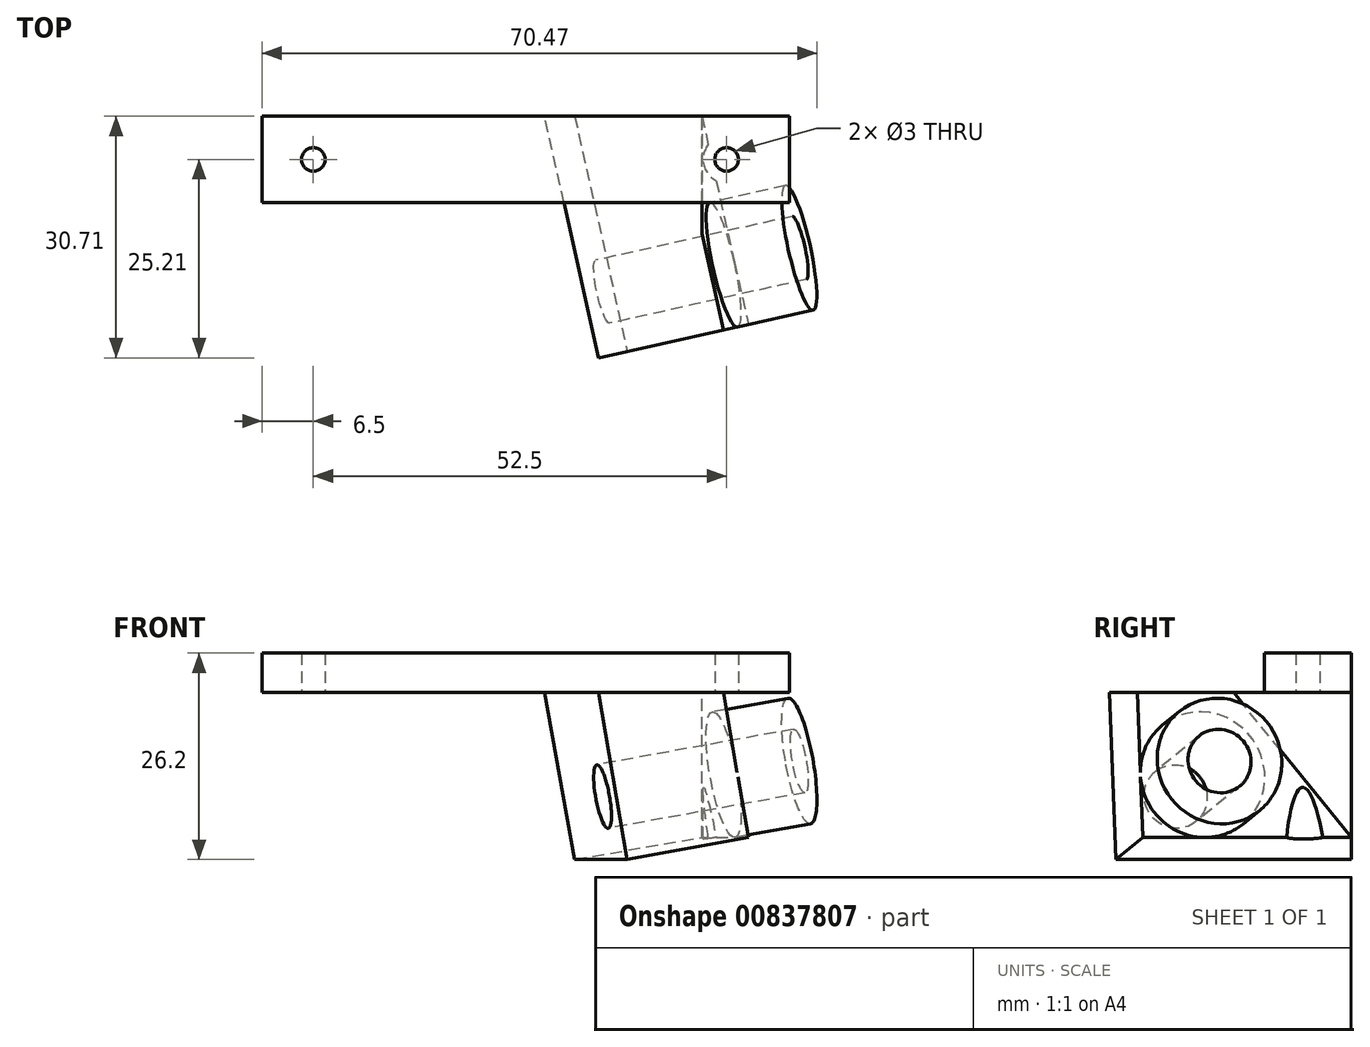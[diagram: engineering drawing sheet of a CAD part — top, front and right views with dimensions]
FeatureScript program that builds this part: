
annotation { "Feature Type Name" : "Feature", "Feature Type Description" : "" }
export const myFeature = defineFeature(function(context is Context, id is Id, definition is map)
    precondition{}
    {
        {
            var Q0;
            Q0=qCreatedBy(makeId("Top.planeOp"),FACE);
            var sketch = newSketch(context, id + "F0", { "sketchPlane" : qUnion([Q0])});
            skLineSegment(sketch, "E0.bottom", {"start": v(37.5, 5.5) * mm, "end": v(-37.5, 5.5) * mm});
            skLineSegment(sketch, "E0.top", {"start": v(37.5, -5.5) * mm, "end": v(-37.5, -5.5) * mm});
            skLineSegment(sketch, "E0.left", {"start": v(37.5, 5.5) * mm, "end": v(37.5, -5.5) * mm});
            skLineSegment(sketch, "E0.right", {"start": v(-37.5, 5.5) * mm, "end": v(-37.5, -5.5) * mm});
            skPoint(sketch, "E0.middle", {"position": v(0, 0) * mm});
            skLineSegment(sketch, "E1", {"start": v(0, 0) * mm, "end": v(-15, 0) * mm, "construction": true});
            skLineSegment(sketch, "E2", {"start": v(0, 0) * mm, "end": v(15, 0) * mm, "construction": true});
            skLineSegment(sketch, "E3", {"start": v(-15, 0) * mm, "end": v(-26.25, 0) * mm, "construction": true});
            skLineSegment(sketch, "E4", {"start": v(15, 0) * mm, "end": v(26.25, 0) * mm, "construction": true});
            skCircle(sketch, "E5", {"center": v(-26.25, 0) * mm, "radius": 1.5 * mm});
            skCircle(sketch, "E6", {"center": v(26.25, 0) * mm, "radius": 1.5 * mm});
            skLineSegment(sketch, "E7", {"start": v(-37.5, 5.5) * mm, "end": v(-43.1, -5.5) * mm, "construction": true});
            skLineSegment(sketch, "E8", {"start": v(-37.5, -5.5) * mm, "end": v(-43.1, -5.5) * mm, "construction": true});
            skLineSegment(sketch, "E9", {"start": v(77.8, 6.5) * mm, "end": v(-101.6, -33.5) * mm, "construction": true});
            skLineSegment(sketch, "E10", {"start": v(-101.6, -33.5) * mm, "end": v(-99.87, -41.3) * mm, "construction": true});
            skLineSegment(sketch, "E11", {"start": v(-99.87, -41.3) * mm, "end": v(79.55, -1.3) * mm, "construction": true});
            skLineSegment(sketch, "E12", {"start": v(77.8, 6.5) * mm, "end": v(79.55, -1.3) * mm, "construction": true});
            skLineSegment(sketch, "E13", {"start": v(24.75, 0) * mm, "end": v(20.75, 0) * mm, "construction": true});
            skLineSegment(sketch, "E14", {"start": v(20.75, 0) * mm, "end": v(23.81, -13.73) * mm, "construction": true});
            skLineSegment(sketch, "E15", {"start": v(20.75, 0) * mm, "end": v(19.52, 5.5) * mm, "construction": true});
            skLineSegment(sketch, "E16", {"start": v(20.75, 0) * mm, "end": v(5.13, -3.48) * mm, "construction": true});
            skLineSegment(sketch, "E17", {"start": v(5.13, -3.48) * mm, "end": v(8.2, -17.2) * mm, "construction": true});
            skLineSegment(sketch, "E18", {"start": v(5.13, -3.48) * mm, "end": v(3.13, 5.5) * mm, "construction": true});
            skLineSegment(sketch, "E19", {"start": v(23.81, -13.73) * mm, "end": v(24.72, -17.82) * mm, "construction": true});
            skLineSegment(sketch, "E20", {"start": v(8.2, -17.2) * mm, "end": v(9.1, -21.3) * mm, "construction": true});
            skLineSegment(sketch, "E21", {"start": v(24.72, -17.82) * mm, "end": v(9.1, -21.3) * mm});
            skLineSegment(sketch, "E22", {"start": v(19.52, 5.5) * mm, "end": v(24.72, -17.82) * mm});
            skLineSegment(sketch, "E23", {"start": v(9.1, -21.3) * mm, "end": v(3.13, 5.5) * mm});
            skLineSegment(sketch, "E24", {"start": v(37.5, 5.5) * mm, "end": v(37.5, 9.6) * mm});
            skLineSegment(sketch, "E25", {"start": v(37.5, 9.6) * mm, "end": v(-37.23, 9.6) * mm});
            skLineSegment(sketch, "E26", {"start": v(-37.23, 9.6) * mm, "end": v(-37.5, 5.5) * mm});
            skCircle(sketch, "E27", {"center": v(26.25, 0) * mm, "radius": 3 * mm});
            skLineSegment(sketch, "E28", {"start": v(29.25, 0) * mm, "end": v(34.25, 0) * mm, "construction": true});
            skLineSegment(sketch, "E29", {"start": v(34.25, 0) * mm, "end": v(34.25, 9.6) * mm, "construction": true});
            skLineSegment(sketch, "E30", {"start": v(34.25, 0) * mm, "end": v(34.25, -5.5) * mm, "construction": true});
            skLineSegment(sketch, "E31", {"start": v(-27.75, 0) * mm, "end": v(-32.75, 0) * mm, "construction": true});
            skLineSegment(sketch, "E32", {"start": v(-32.75, 0) * mm, "end": v(-32.75, 9.6) * mm, "construction": true});
            skLineSegment(sketch, "E33", {"start": v(-32.75, 0) * mm, "end": v(-32.75, -5.5) * mm, "construction": true});
            skLineSegment(sketch, "E34", {"start": v(34.25, 5.5) * mm, "end": v(34.25, -5.5) * mm});
            skLineSegment(sketch, "E35", {"start": v(-32.75, 5.5) * mm, "end": v(-32.75, -5.5) * mm});
            skSolve(sketch);
        }
        {
            var Q0;
            {var subQ5=sQuery(id+"F0.wireOp",EDGE,"E21");Q0=makeQuery(id+"F0.imprint","IMPRINT",FACE,{"disambiguationData":[TD([[makeQuery(id+"F0.imprint","IMPRINT",EDGE,{"derivedFrom":subQ5}),-1.0]])]});}
            var Q1;
            {var subQ0=sQuery(id+"F0.wireOp",EDGE,"E22");var subQ1=sQuery(id+"F0.wireOp",EDGE,"E0.bottom");var subQ2=makeQuery(id+"F0.imprint","INTERSECT",VERTEX,{"derivedFrom":[subQ1,subQ0]});Q1=makeQuery(id+"F0.imprint","IMPRINT",FACE,{"disambiguationData":[TD([[makeQuery(id+"F0.imprint","IMPRINT",EDGE,{"disambiguationData":[TD([[subQ2,-1.0]])],"derivedFrom":subQ1}),1.0]])]});}
            var Q2;
            Q2=makeQuery(id+"F0.imprint","IMPRINT",FACE,{"disambiguationData":[TD([[makeQuery(id+"F0.imprint","IMPRINT",EDGE,{"derivedFrom":sQuery(id+"F0.wireOp",EDGE,"E6")}),-1.0]])]});
            var Q3;
            Q3=makeQuery(id+"F0.imprint","IMPRINT",FACE,{"disambiguationData":[TD([[makeQuery(id+"F0.imprint","IMPRINT",EDGE,{"derivedFrom":sQuery(id+"F0.wireOp",EDGE,"E27")}),-1.0]])]});
            var Q4;
            Q4=makeQuery(id+"F0.imprint","IMPRINT",FACE,{"disambiguationData":[TD([[makeQuery(id+"F0.imprint","IMPRINT",EDGE,{"derivedFrom":sQuery(id+"F0.wireOp",EDGE,"E5")}),-1.0]])]});
            extrude(context, id + "F1", {"entities" : qUnion([Q0, Q1, Q2, Q3, Q4]), "depth" : 5 * mm, "offsetDistance" : 25 * mm});
        }
        {
            var Q0;
            {var subQ0=sQuery(id+"F0.wireOp",EDGE,"E22");var subQ1=sQuery(id+"F0.wireOp",EDGE,"E0.bottom");var subQ2=makeQuery(id+"F0.imprint","INTERSECT",VERTEX,{"derivedFrom":[subQ1,subQ0]});Q0=makeQuery(id+"F0.imprint","IMPRINT",FACE,{"disambiguationData":[TD([[makeQuery(id+"F0.imprint","IMPRINT",EDGE,{"disambiguationData":[TD([[subQ2,-1.0]])],"derivedFrom":subQ1}),1.0]])]});}
            var Q1;
            {var subQ5=sQuery(id+"F0.wireOp",EDGE,"E21");Q1=makeQuery(id+"F0.imprint","IMPRINT",FACE,{"disambiguationData":[TD([[makeQuery(id+"F0.imprint","IMPRINT",EDGE,{"derivedFrom":subQ5}),-1.0]])]});}
            extrude(context, id + "F2", {"entities" : qUnion([Q0, Q1]), "operationType" : NewBodyOperationType.ADD, "oppositeDirection" : true, "depth" : 21.2 * mm, "offsetDistance" : 25 * mm});
        }
        {
            var Q0;
            {var subQ5=sQuery(id+"F0.wireOp",EDGE,"E21");Q0=makeQuery(id+"F0.imprint","IMPRINT",FACE,{"disambiguationData":[TD([[makeQuery(id+"F0.imprint","IMPRINT",EDGE,{"derivedFrom":subQ5}),-1.0]])]});}
            extrude(context, id + "F3", {"entities" : qUnion([Q0]), "operationType" : NewBodyOperationType.REMOVE, "depth" : 5 * mm, "offsetDistance" : 25 * mm});
        }
        {
            var Q0;
            {var subQ0=sQuery(id+"F0.wireOp",EDGE,"E21");Q0=makeQuery(id+"F2.boolean.opBoolean","MERGE",FACE,{"derivedFrom":[makeQuery(id+"F1.opExtrude","SWEPT_FACE",FACE,{"disambiguationData":[OSD([subQ0])]}),makeQuery(id+"F2.opExtrude","SWEPT_FACE",FACE,{"disambiguationData":[OSD([subQ0])]})]});}
            var sketch = newSketch(context, id + "F4", { "sketchPlane" : qUnion([Q0])});
            skLineSegment(sketch, "E36", {"start": v(4.25, 0) * mm, "end": v(8, -21.2) * mm});
            skLineSegment(sketch, "E37", {"start": v(8, -21.2) * mm, "end": v(23.75, -18.42) * mm});
            skLineSegment(sketch, "E38", {"start": v(23.75, -18.42) * mm, "end": v(20.5, 0) * mm});
            skLineSegment(sketch, "E39", {"start": v(20.5, 0) * mm, "end": v(4.25, 0) * mm});
            skSolve(sketch);
        }
        {
            var Q0;
            {var subQ0=sQuery(id+"F4.wireOp",EDGE,"E37");var subQ1=sQuery(id+"F0.wireOp",EDGE,"E21");var subQ2=makeQuery(id+"F2.opExtrude","CAP_EDGE",EDGE,{"disambiguationData":[OSD([subQ1])],"isStart":false});var subQ3=makeQuery(id+"F4.imprint","INTERSECT",VERTEX,{"derivedFrom":[subQ2,sQuery(id+"F4.wireOp",EDGE,"E36"),subQ0]});Q0=makeQuery(id+"F4.imprint","IMPRINT",FACE,{"disambiguationData":[TD([[makeQuery(id+"F4.imprint","IMPRINT",EDGE,{"disambiguationData":[TD([[subQ3,-1.0]])],"derivedFrom":subQ0}),-1.0]])]});}
            var Q1;
            {var subQ0=sQuery(id+"F4.wireOp",EDGE,"E36");Q1=makeQuery(id+"F4.imprint","IMPRINT",FACE,{"disambiguationData":[TD([[makeQuery(id+"F4.imprint","IMPRINT",EDGE,{"derivedFrom":subQ0}),-1.0]])]});}
            extrude(context, id + "F5", {"entities" : qUnion([Q0, Q1]), "operationType" : NewBodyOperationType.REMOVE, "oppositeDirection" : true, "depth" : 30 * mm, "offsetDistance" : 25 * mm});
        }
        {
            var Q0;
            {var subQ0=sQuery(id+"F4.wireOp",EDGE,"E38");Q0=makeQuery(id+"F4.imprint","IMPRINT",FACE,{"disambiguationData":[TD([[makeQuery(id+"F4.imprint","IMPRINT",EDGE,{"derivedFrom":subQ0}),1.0]])]});}
            extrude(context, id + "F6", {"entities" : qUnion([Q0]), "operationType" : NewBodyOperationType.ADD, "oppositeDirection" : true, "depth" : 23.9 * mm, "offsetDistance" : 25 * mm});
        }
        {
            var Q0;
            {var subQ4=sQuery(id+"F0.wireOp",EDGE,"E24");Q0=makeQuery(id+"F0.imprint","IMPRINT",FACE,{"disambiguationData":[TD([[makeQuery(id+"F0.imprint","IMPRINT",EDGE,{"derivedFrom":subQ4}),1.0]])]});}
            extrude(context, id + "F7", {"entities" : qUnion([Q0]), "operationType" : NewBodyOperationType.REMOVE, "oppositeDirection" : true, "depth" : 25 * mm, "offsetDistance" : 25 * mm});
        }
        {
            var Q0;
            Q0=makeQuery(id+"F0.imprint","IMPRINT",FACE,{"disambiguationData":[TD([[makeQuery(id+"F0.imprint","IMPRINT",EDGE,{"derivedFrom":sQuery(id+"F0.wireOp",EDGE,"E6")}),-1.0]])]});
            var Q1;
            Q1=makeQuery(id+"F0.imprint","IMPRINT",FACE,{"disambiguationData":[TD([[makeQuery(id+"F0.imprint","IMPRINT",EDGE,{"derivedFrom":sQuery(id+"F0.wireOp",EDGE,"E6")}),1.0]])]});
            extrude(context, id + "F8", {"entities" : qUnion([Q0, Q1]), "operationType" : NewBodyOperationType.REMOVE, "oppositeDirection" : true, "depth" : 25 * mm, "offsetDistance" : 25 * mm});
        }
        {
            var Q0;
            {var subQ0=sQuery(id+"F4.wireOp",EDGE,"E36");Q0=makeQuery(id+"F4.imprint","IMPRINT",FACE,{"disambiguationData":[TD([[makeQuery(id+"F4.imprint","IMPRINT",EDGE,{"derivedFrom":subQ0}),1.0]])]});}
            var Q1;
            {var subQ0=sQuery(id+"F4.wireOp",EDGE,"E38");Q1=makeQuery(id+"F4.imprint","IMPRINT",FACE,{"disambiguationData":[TD([[makeQuery(id+"F4.imprint","IMPRINT",EDGE,{"derivedFrom":subQ0}),1.0]])]});}
            extrude(context, id + "F9", {"entities" : qUnion([Q0, Q1]), "operationType" : NewBodyOperationType.ADD, "depth" : 4 * mm, "offsetDistance" : 25 * mm});
        }
        {
            var Q0;
            {var subQ0=sQuery(id+"F4.wireOp",EDGE,"E38");Q0=makeQuery(id+"F9.boolean.opBoolean","MERGE",FACE,{"derivedFrom":[makeQuery(id+"F6.opExtrude","SWEPT_FACE",FACE,{"disambiguationData":[OSD([subQ0])]}),makeQuery(id+"F9.opExtrude","SWEPT_FACE",FACE,{"disambiguationData":[OSD([subQ0])]})]});}
            var sketch = newSketch(context, id + "F10", { "sketchPlane" : qUnion([Q0])});
            skLineSegment(sketch, "E40", {"start": v(-18.53, -4.28) * mm, "end": v(-17.8, -22.97) * mm, "construction": true});
            skLineSegment(sketch, "E41", {"start": v(-17.8, -22.97) * mm, "end": v(-18.12, -14.88) * mm, "construction": true});
            skLineSegment(sketch, "E42", {"start": v(-18.12, -14.88) * mm, "end": v(-26.22, -14.88) * mm, "construction": true});
            skCircle(sketch, "E43", {"center": v(-18.12, -14.88) * mm, "radius": 8.1 * mm});
            skCircle(sketch, "E44", {"center": v(-18.12, -14.88) * mm, "radius": 4.1 * mm});
            skSolve(sketch);
        }
        {
            var Q0;
            Q0=qSketchRegion(id+"F10",true);
            extrude(context, id + "F11", {"entities" : qUnion([Q0]), "operationType" : NewBodyOperationType.ADD, "depth" : 10 * mm, "offsetDistance" : 25 * mm});
        }
        {
            var Q0;
            {var subQ0=sQuery(id+"F4.wireOp",EDGE,"E38");Q0=makeQuery(id+"F11.boolean.opBoolean","SPLIT",FACE,{"disambiguationData":[TD([makeQuery(id+"F11.opExtrude","SWEPT_FACE",FACE,{"disambiguationData":[OSD([sQuery(id+"F10.wireOp",EDGE,"E44")])]})])],"derivedFrom":makeQuery(id+"F9.boolean.opBoolean","MERGE",FACE,{"derivedFrom":[makeQuery(id+"F6.opExtrude","SWEPT_FACE",FACE,{"disambiguationData":[OSD([subQ0])]}),makeQuery(id+"F9.opExtrude","SWEPT_FACE",FACE,{"disambiguationData":[OSD([subQ0])]})]})});}
            extrude(context, id + "F12", {"entities" : qUnion([Q0]), "operationType" : NewBodyOperationType.REMOVE, "oppositeDirection" : true, "depth" : 25 * mm, "offsetDistance" : 25 * mm});
        }
        {
            var Q0;
            {var subQ0=sQuery(id+"F0.wireOp",EDGE,"E0.bottom");Q0=makeQuery(id+"F7.boolean.opBoolean","MERGE",FACE,{"derivedFrom":[makeQuery(id+"F2.boolean.opBoolean","MERGE",FACE,{"derivedFrom":[makeQuery(id+"F1.opExtrude","SWEPT_FACE",FACE,{"disambiguationData":[OSD([subQ0])]}),makeQuery(id+"F2.opExtrude","SWEPT_FACE",FACE,{"disambiguationData":[OSD([subQ0])]})]})],"fromTools":[makeQuery(id+"F7.opExtrude","SWEPT_FACE",FACE,{"disambiguationData":[OSD([subQ0])]})]});}
            var sketch = newSketch(context, id + "F13", { "sketchPlane" : qUnion([Q0])});
            skLineSegment(sketch, "E45", {"start": v(-23.1, -18.42) * mm, "end": v(-23.1, 0) * mm});
            skSolve(sketch);
        }
        {
            var Q0;
            {var subQ0=sQuery(id+"F13.wireOp",EDGE,"E45");Q0=makeQuery(id+"F13.imprint","IMPRINT",FACE,{"disambiguationData":[TD([[makeQuery(id+"F13.imprint","IMPRINT",EDGE,{"derivedFrom":subQ0}),-1.0]])]});}
            extrude(context, id + "F14", {"entities" : qUnion([Q0]), "operationType" : NewBodyOperationType.ADD, "oppositeDirection" : true, "depth" : 15 * mm, "offsetDistance" : 25 * mm});
        }
    });
